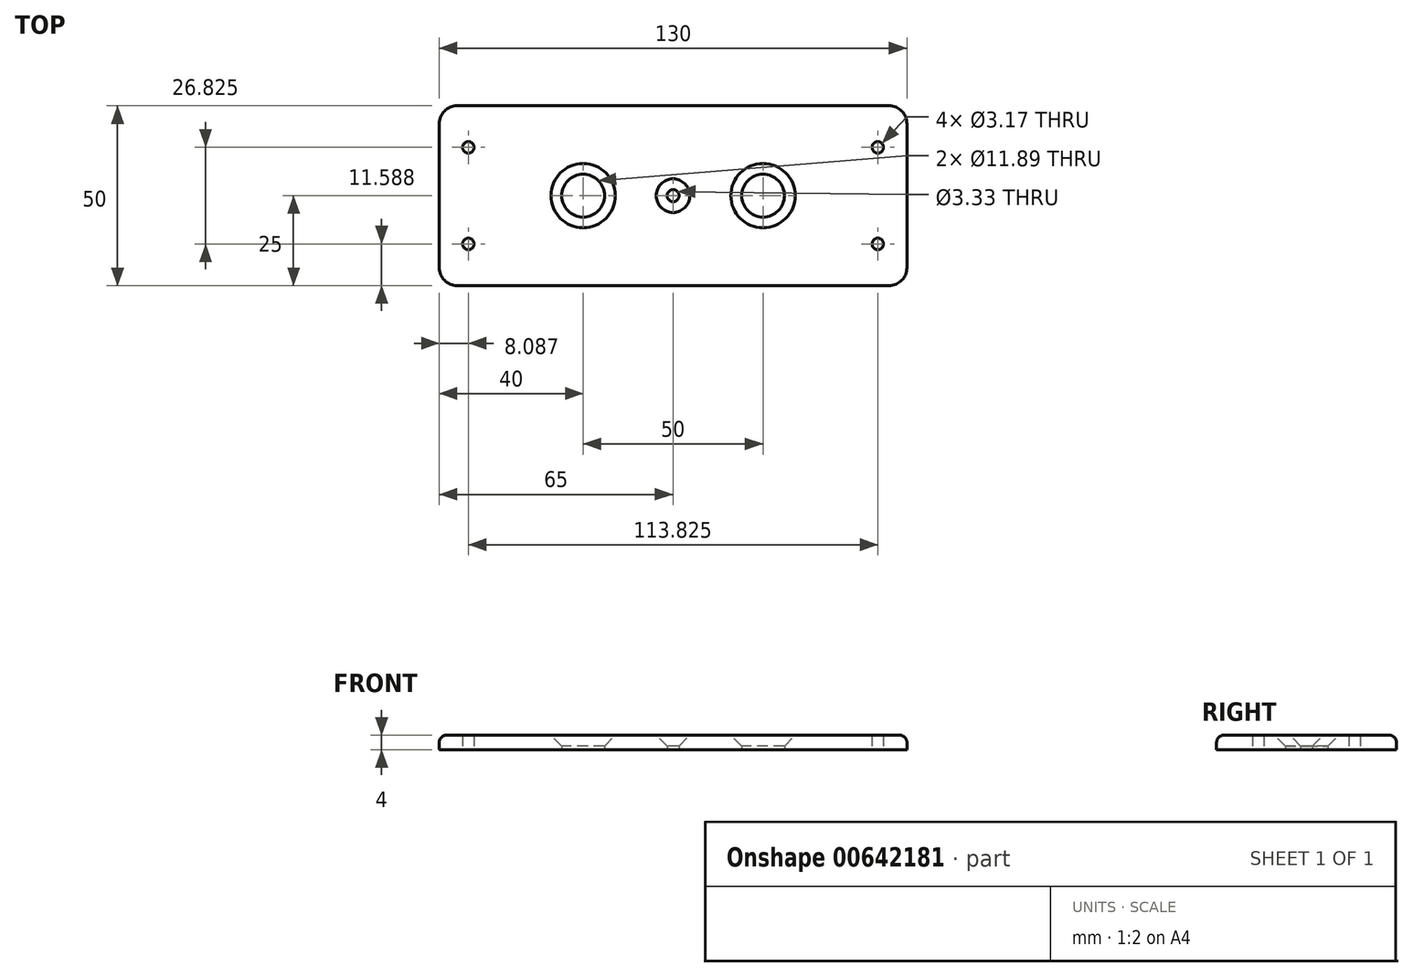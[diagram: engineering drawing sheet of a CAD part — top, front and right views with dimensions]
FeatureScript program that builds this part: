
annotation { "Feature Type Name" : "Feature", "Feature Type Description" : "" }
export const myFeature = defineFeature(function(context is Context, id is Id, definition is map)
    precondition{}
    {
        {
            var Q0;
            Q0=qCreatedBy(makeId("Top.planeOp"),FACE);
            var sketch = newSketch(context, id + "F0", { "sketchPlane" : qUnion([Q0])});
            skLineSegment(sketch, "E0.bottom", {"start": v(65, 25) * mm, "end": v(-65, 25) * mm});
            skLineSegment(sketch, "E0.top", {"start": v(65, -25) * mm, "end": v(-65, -25) * mm});
            skLineSegment(sketch, "E0.left", {"start": v(65, 25) * mm, "end": v(65, -25) * mm});
            skLineSegment(sketch, "E0.right", {"start": v(-65, 25) * mm, "end": v(-65, -25) * mm});
            skPoint(sketch, "E0.middle", {"position": v(0, 0) * mm});
            skLineSegment(sketch, "E1.bottom", {"start": v(-33, 25) * mm, "end": v(33, 25) * mm});
            skSolve(sketch);
        }
        {
            var Q0;
            Q0 = qSketchRegion(id + "F0", true);
            extrude(context, id + "F1", {"entities" : qUnion([Q0]), "depth" : 4 * mm, "offsetDistance" : 25 * mm});
        }
        {
            var Q0;
            Q0=qCreatedBy(makeId("Top.planeOp"),FACE);
            var sketch = newSketch(context, id + "F2", { "sketchPlane" : qUnion([Q0])});
            skLineSegment(sketch, "E2", {"start": v(-46.18, 0) * mm, "end": v(51.18, 0) * mm, "construction": true});
            skCircle(sketch, "E3", {"center": v(-25, 0) * mm, "radius": 5.94 * mm});
            skCircle(sketch, "E4", {"center": v(0, 0) * mm, "radius": 1.66 * mm});
            skLineSegment(sketch, "E5", {"start": v(0, 0) * mm, "end": v(0, 29.56) * mm, "construction": true});
            skCircle(sketch, "E6.MirrorC", {"center": v(25, 0) * mm, "radius": 5.94 * mm});
            skCircle(sketch, "E7", {"center": v(-56.91, 13.41) * mm, "radius": 1.59 * mm});
            skCircle(sketch, "E8.MirrorC", {"center": v(-56.91, -13.41) * mm, "radius": 1.59 * mm});
            skCircle(sketch, "E9.MirrorC", {"center": v(56.91, 13.41) * mm, "radius": 1.59 * mm});
            skCircle(sketch, "E10.MirrorC", {"center": v(56.91, -13.41) * mm, "radius": 1.59 * mm});
            skSolve(sketch);
        }
        {
            var Q0;
            Q0 = qSketchRegion(id + "F2", true);
            extrude(context, id + "F3", {"entities" : qUnion([Q0]), "operationType" : NewBodyOperationType.REMOVE, "depth" : 25 * mm, "offsetDistance" : 25 * mm});
        }
        {
            var Q0;
            Q0=makeQuery(id+"F1.opExtrude","SWEPT_EDGE",EDGE,{"disambiguationData":[OSD([sQuery(id+"F0.wireOp",EDGE,"E0.top"),sQuery(id+"F0.wireOp",EDGE,"E0.right")])]});
            var Q1;
            Q1=makeQuery(id+"F1.opExtrude","SWEPT_EDGE",EDGE,{"disambiguationData":[OSD([sQuery(id+"F0.wireOp",EDGE,"E0.top"),sQuery(id+"F0.wireOp",EDGE,"E0.left")])]});
            var Q2;
            Q2=makeQuery(id+"F1.opExtrude","SWEPT_EDGE",EDGE,{"disambiguationData":[OSD([sQuery(id+"F0.wireOp",EDGE,"E0.bottom"),sQuery(id+"F0.wireOp",EDGE,"E0.left")])]});
            var Q3;
            Q3=makeQuery(id+"F1.opExtrude","SWEPT_EDGE",EDGE,{"disambiguationData":[OSD([sQuery(id+"F0.wireOp",EDGE,"E1.top"),sQuery(id+"F0.wireOp",EDGE,"E1.left")])]});
            var Q4;
            Q4=makeQuery(id+"F1.opExtrude","SWEPT_EDGE",EDGE,{"disambiguationData":[OSD([sQuery(id+"F0.wireOp",EDGE,"E1.top"),sQuery(id+"F0.wireOp",EDGE,"E1.right")])]});
            var Q5;
            Q5=makeQuery(id+"F1.opExtrude","SWEPT_EDGE",EDGE,{"disambiguationData":[OSD([sQuery(id+"F0.wireOp",EDGE,"E0.bottom"),sQuery(id+"F0.wireOp",EDGE,"E0.right")])]});
            fillet(context, id + "F4", {"entities" : qUnion([Q0, Q1, Q2, Q3, Q4, Q5]), "radius" : 5 * mm, "tangentPropagation" : true, "allowEdgeOverflow" : false});
        }
        {
            var Q0;
            Q0=makeQuery(id+"F1.opExtrude","CAP_EDGE",EDGE,{"disambiguationData":[OSD([sQuery(id+"F0.wireOp",EDGE,"E0.right")])],"isStart":false});
            var Q1;
            Q1=makeQuery(id+"F1.opExtrude","CAP_EDGE",EDGE,{"disambiguationData":[OSD([sQuery(id+"F0.wireOp",EDGE,"E1.left")])],"isStart":false});
            fillet(context, id + "F5", {"entities" : qUnion([Q0, Q1]), "radius" : 2 * mm, "tangentPropagation" : true, "allowEdgeOverflow" : false});
        }
        {
            var Q0;
            Q0=makeQuery(id+"F3.boolean.opBoolean","INTERSECT",EDGE,{"derivedFrom":[makeQuery(id+"F1.opExtrude","CAP_FACE",FACE,{"disambiguationData":[OSD([sQuery(id+"F0.wireOp",EDGE,"E0.bottom"),sQuery(id+"F0.wireOp",EDGE,"E0.top"),sQuery(id+"F0.wireOp",EDGE,"E0.left"),sQuery(id+"F0.wireOp",EDGE,"E0.right"),sQuery(id+"F0.wireOp",EDGE,"E1.top"),sQuery(id+"F0.wireOp",EDGE,"E1.left"),sQuery(id+"F0.wireOp",EDGE,"E1.right")])],"isStart":false}),makeQuery(id+"F3.opExtrude","SWEPT_FACE",FACE,{"disambiguationData":[OSD([sQuery(id+"F2.wireOp",EDGE,"E3")])]})]});
            var Q1;
            Q1=makeQuery(id+"F3.boolean.opBoolean","INTERSECT",EDGE,{"derivedFrom":[makeQuery(id+"F1.opExtrude","CAP_FACE",FACE,{"disambiguationData":[OSD([sQuery(id+"F0.wireOp",EDGE,"E0.bottom"),sQuery(id+"F0.wireOp",EDGE,"E0.top"),sQuery(id+"F0.wireOp",EDGE,"E0.left"),sQuery(id+"F0.wireOp",EDGE,"E0.right"),sQuery(id+"F0.wireOp",EDGE,"E1.top"),sQuery(id+"F0.wireOp",EDGE,"E1.left"),sQuery(id+"F0.wireOp",EDGE,"E1.right")])],"isStart":false}),makeQuery(id+"F3.opExtrude","SWEPT_FACE",FACE,{"disambiguationData":[OSD([sQuery(id+"F2.wireOp",EDGE,"E6.MirrorC")])]})]});
            chamfer(context, id + "F6", {"entities" : qUnion([Q0, Q1]), "width" : 3 * mm, "tangentPropagation" : true});
        }
        {
            var Q0;
            Q0=makeQuery(id+"F3.boolean.opBoolean","INTERSECT",EDGE,{"derivedFrom":[makeQuery(id+"F1.opExtrude","CAP_FACE",FACE,{"disambiguationData":[OSD([sQuery(id+"F0.wireOp",EDGE,"E0.bottom"),sQuery(id+"F0.wireOp",EDGE,"E0.top"),sQuery(id+"F0.wireOp",EDGE,"E0.left"),sQuery(id+"F0.wireOp",EDGE,"E0.right"),sQuery(id+"F0.wireOp",EDGE,"E1.top"),sQuery(id+"F0.wireOp",EDGE,"E1.left"),sQuery(id+"F0.wireOp",EDGE,"E1.right")])],"isStart":false}),makeQuery(id+"F3.opExtrude","SWEPT_FACE",FACE,{"disambiguationData":[OSD([sQuery(id+"F2.wireOp",EDGE,"E4")])]})]});
            chamfer(context, id + "F7", {"entities" : qUnion([Q0]), "width" : 3 * mm, "tangentPropagation" : true});
        }
    });
